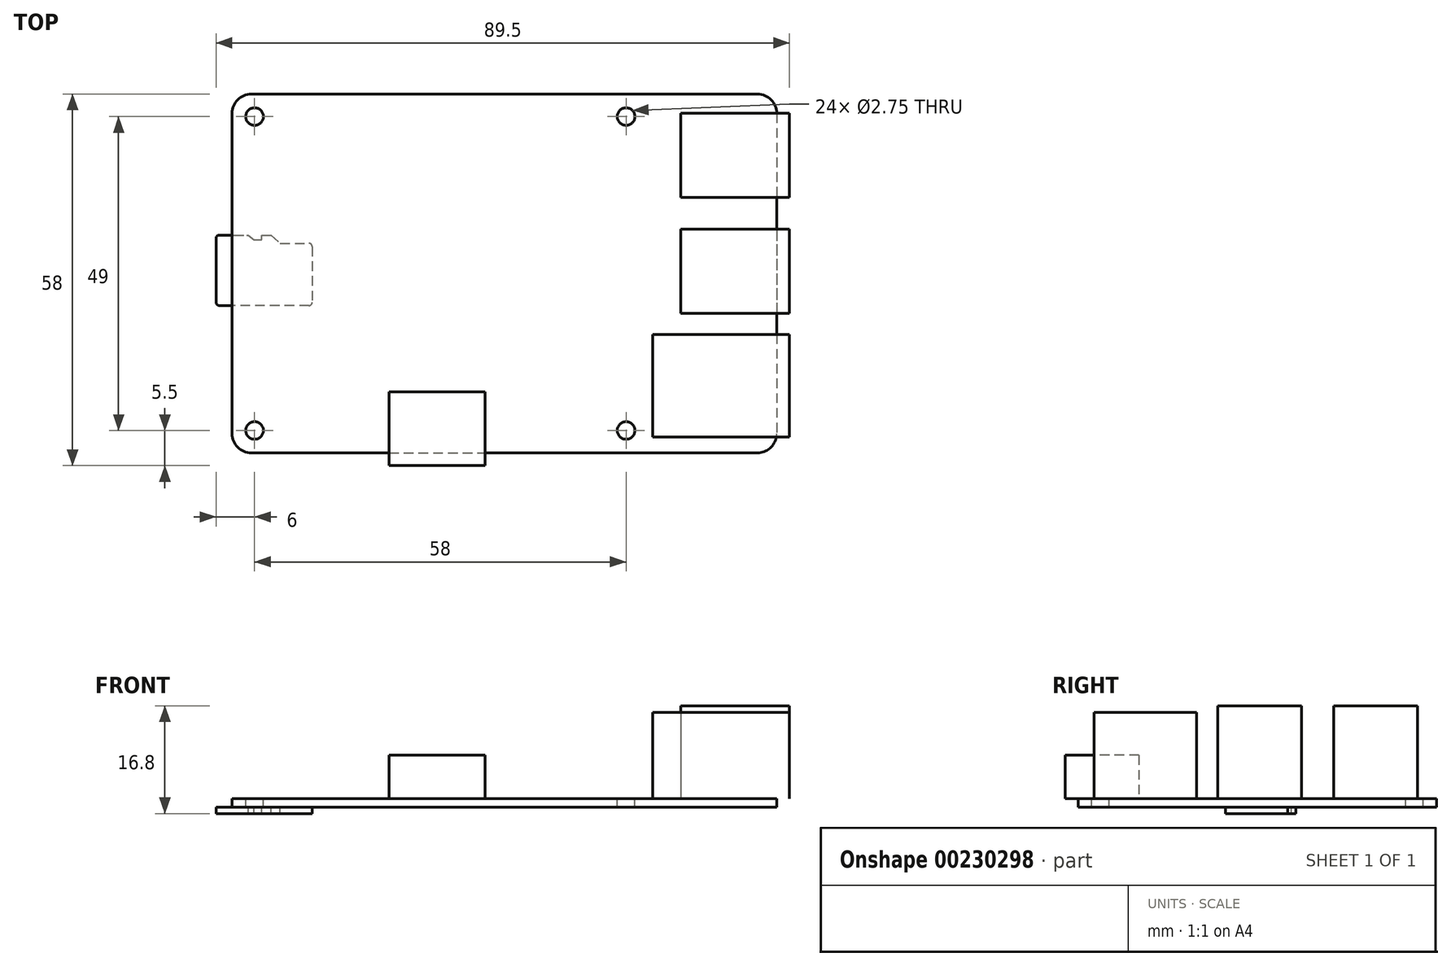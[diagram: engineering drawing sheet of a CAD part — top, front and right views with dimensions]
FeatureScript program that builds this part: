
annotation { "Feature Type Name" : "Feature", "Feature Type Description" : "" }
export const myFeature = defineFeature(function(context is Context, id is Id, definition is map)
    precondition{}
    {
        {
            var Q0;
            Q0=qCreatedBy(makeId("Top.planeOp"),FACE);
            var sketch = newSketch(context, id + "F0", { "sketchPlane" : qUnion([Q0])});
            skLineSegment(sketch, "E0.bottom", {"start": v(-39.5, 28) * mm, "end": v(39.5, 28) * mm});
            skLineSegment(sketch, "E0.top", {"start": v(-39.5, -28) * mm, "end": v(39.5, -28) * mm});
            skLineSegment(sketch, "E0.left", {"start": v(-42.5, 25) * mm, "end": v(-42.5, -25) * mm});
            skLineSegment(sketch, "E0.right", {"start": v(42.5, 25) * mm, "end": v(42.5, -25) * mm});
            skPoint(sketch, "E1", {"position": v(-42.5, 0) * mm});
            skPoint(sketch, "E2", {"position": v(0, 28) * mm});
            skPoint(sketch, "E3.visualSharp", {"position": v(-42.5, 28) * mm});
            skArc(sketch, "E3.filletArc", {"start": v(-39.5, 28) * mm, "mid": v(-41.62, 27.12) * mm, "end": v(-42.5, 25) * mm});
            skPoint(sketch, "E4.visualSharp", {"position": v(42.5, 28) * mm});
            skArc(sketch, "E4.filletArc", {"start": v(42.5, 25) * mm, "mid": v(41.62, 27.12) * mm, "end": v(39.5, 28) * mm});
            skPoint(sketch, "E5.visualSharp", {"position": v(42.5, -28) * mm});
            skArc(sketch, "E5.filletArc", {"start": v(39.5, -28) * mm, "mid": v(41.62, -27.12) * mm, "end": v(42.5, -25) * mm});
            skPoint(sketch, "E6.visualSharp", {"position": v(-42.5, -28) * mm});
            skArc(sketch, "E6.filletArc", {"start": v(-42.5, -25) * mm, "mid": v(-41.62, -27.12) * mm, "end": v(-39.5, -28) * mm});
            skSolve(sketch);
        }
        {
            var Q0;
            Q0=makeQuery(id+"F0.imprint","IMPRINT",FACE,{"disambiguationData":[TD([[makeQuery(id+"F0.imprint","IMPRINT",EDGE,{"derivedFrom":sQuery(id+"F0.wireOp",EDGE,"E0.bottom")}),-1.0]])]});
            extrude(context, id + "F1", {"entities" : qUnion([Q0]), "depth" : 1.3 * mm});
        }
        {
            var Q0;
            Q0=makeQuery(id+"F1.opExtrude","CAP_FACE",FACE,{"disambiguationData":[OSD([sQuery(id+"F0.wireOp",EDGE,"E0.bottom"),sQuery(id+"F0.wireOp",EDGE,"E0.top"),sQuery(id+"F0.wireOp",EDGE,"E0.left"),sQuery(id+"F0.wireOp",EDGE,"E0.right")])],"isStart":false});
            var sketch = newSketch(context, id + "F2", { "sketchPlane" : qUnion([Q0])});
            skCircle(sketch, "E7", {"center": v(-39, 24.5) * mm, "radius": 1.38 * mm});
            skCircle(sketch, "E8", {"center": v(19, 24.5) * mm, "radius": 1.38 * mm});
            skCircle(sketch, "E9", {"center": v(-39, -24.5) * mm, "radius": 1.38 * mm});
            skCircle(sketch, "E10", {"center": v(19, -24.5) * mm, "radius": 1.38 * mm});
            skSolve(sketch);
        }
        {
            var Q0;
            Q0 = qSketchRegion(id + "F2", true);
            extrude(context, id + "F3", {"entities" : qUnion([Q0]), "operationType" : NewBodyOperationType.REMOVE, "endBound" : BoundingType.UP_TO_NEXT, "oppositeDirection" : true, "depth" : 25 * mm});
        }
        {
            var Q0;
            Q0=makeQuery(id+"F1.opExtrude","CAP_FACE",FACE,{"disambiguationData":[OSD([sQuery(id+"F0.wireOp",EDGE,"E0.bottom"),sQuery(id+"F0.wireOp",EDGE,"E0.top"),sQuery(id+"F0.wireOp",EDGE,"E0.left"),sQuery(id+"F0.wireOp",EDGE,"E0.right"),sQuery(id+"F0.wireOp",EDGE,"E3.filletArc"),sQuery(id+"F0.wireOp",EDGE,"E4.filletArc"),sQuery(id+"F0.wireOp",EDGE,"E5.filletArc"),sQuery(id+"F0.wireOp",EDGE,"E6.filletArc")])],"isStart":false});
            var sketch = newSketch(context, id + "F4", { "sketchPlane" : qUnion([Q0])});
            skLineSegment(sketch, "E11.bottom", {"start": v(23.15, -9.5) * mm, "end": v(44.5, -9.5) * mm});
            skLineSegment(sketch, "E11.top", {"start": v(23.15, -25.5) * mm, "end": v(44.5, -25.5) * mm});
            skLineSegment(sketch, "E11.left", {"start": v(23.15, -9.5) * mm, "end": v(23.15, -25.5) * mm});
            skLineSegment(sketch, "E11.right", {"start": v(44.5, -9.5) * mm, "end": v(44.5, -25.5) * mm});
            skSolve(sketch);
        }
        {
            var Q0;
            Q0 = qSketchRegion(id + "F4", true);
            extrude(context, id + "F5", {"entities" : qUnion([Q0]), "depth" : 13.5 * mm});
        }
        {
            var Q0;
            Q0=makeQuery(id+"F1.opExtrude","CAP_FACE",FACE,{"disambiguationData":[OSD([sQuery(id+"F0.wireOp",EDGE,"E0.bottom"),sQuery(id+"F0.wireOp",EDGE,"E0.top"),sQuery(id+"F0.wireOp",EDGE,"E0.left"),sQuery(id+"F0.wireOp",EDGE,"E0.right"),sQuery(id+"F0.wireOp",EDGE,"E3.filletArc"),sQuery(id+"F0.wireOp",EDGE,"E4.filletArc"),sQuery(id+"F0.wireOp",EDGE,"E5.filletArc"),sQuery(id+"F0.wireOp",EDGE,"E6.filletArc")])],"isStart":false});
            var sketch = newSketch(context, id + "F6", { "sketchPlane" : qUnion([Q0])});
            skLineSegment(sketch, "E12.bottom", {"start": v(27.5, 6.9) * mm, "end": v(44.5, 6.9) * mm});
            skLineSegment(sketch, "E12.top", {"start": v(27.5, -6.2) * mm, "end": v(44.5, -6.2) * mm});
            skLineSegment(sketch, "E12.left", {"start": v(27.5, 6.9) * mm, "end": v(27.5, -6.2) * mm});
            skLineSegment(sketch, "E12.right", {"start": v(44.5, 6.9) * mm, "end": v(44.5, -6.2) * mm});
            skLineSegment(sketch, "E13.bottom", {"start": v(27.5, 25) * mm, "end": v(44.5, 25) * mm});
            skLineSegment(sketch, "E13.top", {"start": v(27.5, 11.9) * mm, "end": v(44.5, 11.9) * mm});
            skLineSegment(sketch, "E13.left", {"start": v(27.5, 25) * mm, "end": v(27.5, 11.9) * mm});
            skLineSegment(sketch, "E13.right", {"start": v(44.5, 25) * mm, "end": v(44.5, 11.9) * mm});
            skSolve(sketch);
        }
        {
            var Q0;
            Q0 = qSketchRegion(id + "F6", true);
            extrude(context, id + "F7", {"entities" : qUnion([Q0]), "depth" : 14.5 * mm});
        }
        {
            var Q0;
            Q0=makeQuery(id+"F1.opExtrude","CAP_FACE",FACE,{"disambiguationData":[OSD([sQuery(id+"F0.wireOp",EDGE,"E0.bottom"),sQuery(id+"F0.wireOp",EDGE,"E0.top"),sQuery(id+"F0.wireOp",EDGE,"E0.left"),sQuery(id+"F0.wireOp",EDGE,"E0.right"),sQuery(id+"F0.wireOp",EDGE,"E3.filletArc"),sQuery(id+"F0.wireOp",EDGE,"E4.filletArc"),sQuery(id+"F0.wireOp",EDGE,"E5.filletArc"),sQuery(id+"F0.wireOp",EDGE,"E6.filletArc")])],"isStart":false});
            var sketch = newSketch(context, id + "F8", { "sketchPlane" : qUnion([Q0])});
            skLineSegment(sketch, "E14.bottom", {"start": v(-18, -18.5) * mm, "end": v(-3, -18.5) * mm});
            skLineSegment(sketch, "E14.top", {"start": v(-18, -30) * mm, "end": v(-3, -30) * mm});
            skLineSegment(sketch, "E14.left", {"start": v(-18, -18.5) * mm, "end": v(-18, -30) * mm});
            skLineSegment(sketch, "E14.right", {"start": v(-3, -18.5) * mm, "end": v(-3, -30) * mm});
            skPoint(sketch, "E15", {"position": v(-10.5, -30) * mm});
            skSolve(sketch);
        }
        {
            var Q0;
            Q0 = qSketchRegion(id + "F8", true);
            extrude(context, id + "F9", {"entities" : qUnion([Q0]), "depth" : 6.8 * mm});
        }
        {
            var Q0;
            Q0=makeQuery(id+"F1.opExtrude","CAP_FACE",FACE,{"disambiguationData":[OSD([sQuery(id+"F0.wireOp",EDGE,"E0.bottom"),sQuery(id+"F0.wireOp",EDGE,"E0.top"),sQuery(id+"F0.wireOp",EDGE,"E0.left"),sQuery(id+"F0.wireOp",EDGE,"E0.right"),sQuery(id+"F0.wireOp",EDGE,"E3.filletArc"),sQuery(id+"F0.wireOp",EDGE,"E4.filletArc"),sQuery(id+"F0.wireOp",EDGE,"E5.filletArc"),sQuery(id+"F0.wireOp",EDGE,"E6.filletArc")])],"isStart":true});
            var sketch = newSketch(context, id + "F10", { "sketchPlane" : qUnion([Q0])});
            skLineSegment(sketch, "E16", {"start": v(-45, 4.5) * mm, "end": v(-45, -5.5) * mm});
            skLineSegment(sketch, "E17", {"start": v(-44.5, -6) * mm, "end": v(-40, -6) * mm});
            skLineSegment(sketch, "E18", {"start": v(-40, -6) * mm, "end": v(-39.1, -5.3) * mm});
            skLineSegment(sketch, "E19", {"start": v(-39.1, -5.3) * mm, "end": v(-37.9, -5.3) * mm});
            skLineSegment(sketch, "E20", {"start": v(-37.9, -5.3) * mm, "end": v(-37.9, -6) * mm});
            skLineSegment(sketch, "E21", {"start": v(-37.9, -6) * mm, "end": v(-36.4, -6) * mm});
            skLineSegment(sketch, "E22", {"start": v(-36.4, -6) * mm, "end": v(-35, -4.7) * mm});
            skLineSegment(sketch, "E23", {"start": v(-35, -4.7) * mm, "end": v(-30.5, -4.7) * mm});
            skLineSegment(sketch, "E24", {"start": v(-30, -4.2) * mm, "end": v(-30, 4.5) * mm});
            skLineSegment(sketch, "E25", {"start": v(-30.5, 5) * mm, "end": v(-44.5, 5) * mm});
            skPoint(sketch, "E26.visualSharp", {"position": v(-45, 5) * mm});
            skArc(sketch, "E26.filletArc", {"start": v(-44.5, 5) * mm, "mid": v(-44.85, 4.85) * mm, "end": v(-45, 4.5) * mm});
            skPoint(sketch, "E27.visualSharp", {"position": v(-30, 5) * mm});
            skArc(sketch, "E27.filletArc", {"start": v(-30, 4.5) * mm, "mid": v(-30.15, 4.85) * mm, "end": v(-30.5, 5) * mm});
            skPoint(sketch, "E28.visualSharp", {"position": v(-30, -4.7) * mm});
            skArc(sketch, "E28.filletArc", {"start": v(-30.5, -4.7) * mm, "mid": v(-30.15, -4.55) * mm, "end": v(-30, -4.2) * mm});
            skPoint(sketch, "E29.visualSharp", {"position": v(-45, -6) * mm});
            skArc(sketch, "E29.filletArc", {"start": v(-45, -5.5) * mm, "mid": v(-44.85, -5.85) * mm, "end": v(-44.5, -6) * mm});
            skSolve(sketch);
        }
        {
            var Q0;
            Q0 = qSketchRegion(id + "F10", true);
            extrude(context, id + "F11", {"entities" : qUnion([Q0]), "depth" : 1 * mm});
        }
    });
